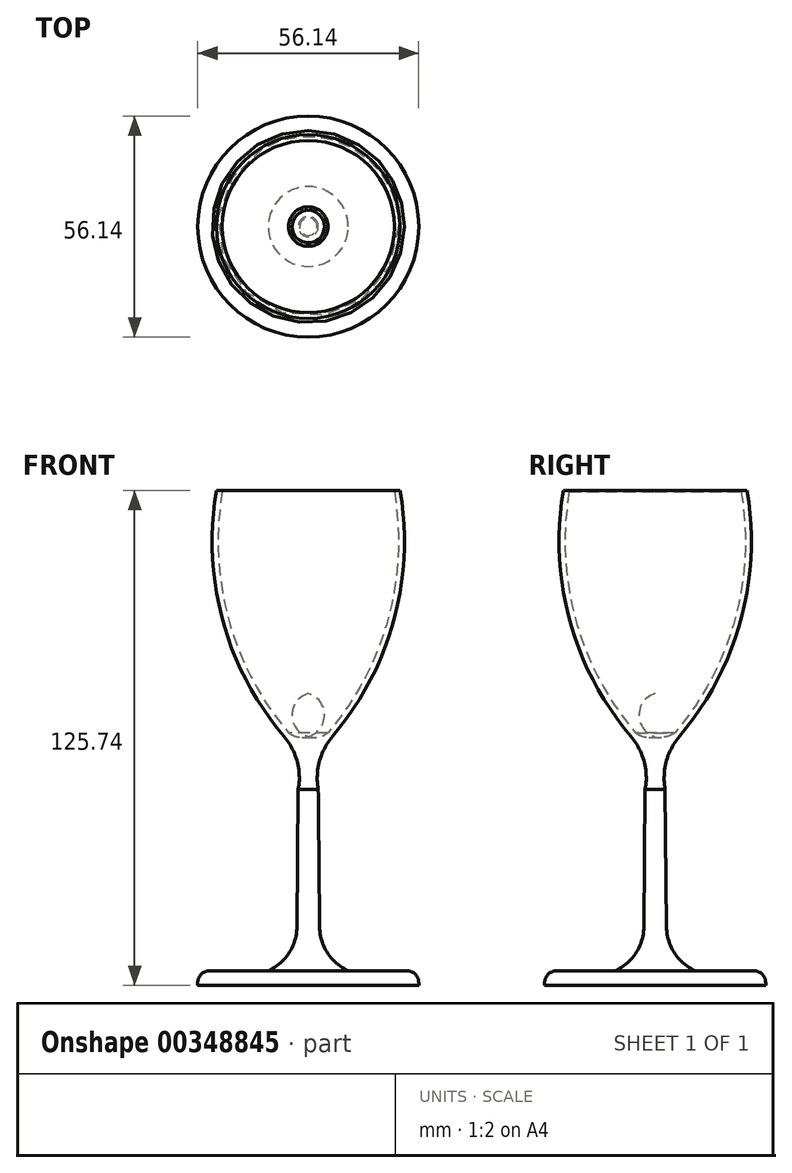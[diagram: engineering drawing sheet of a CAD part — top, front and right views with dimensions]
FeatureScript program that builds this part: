
annotation { "Feature Type Name" : "Feature", "Feature Type Description" : "" }
export const myFeature = defineFeature(function(context is Context, id is Id, definition is map)
    precondition{}
    {
        {
            var Q0;
            Q0=qCreatedBy(makeId("Front.planeOp"),FACE);
            var sketch = newSketch(context, id + "F0", { "sketchPlane" : qUnion([Q0])});
            skArc(sketch, "E0", {"start": v(6.16, -12.1) * mm, "mid": v(21.68, 17.25) * mm, "end": v(23.33, 50.4) * mm});
            skArc(sketch, "E1", {"start": v(6.16, -12.1) * mm, "mid": v(2.83, -18.42) * mm, "end": v(2.54, -25.57) * mm});
            skLineSegment(sketch, "E2", {"start": v(2.88, -60.4) * mm, "end": v(2.54, -25.57) * mm});
            skArc(sketch, "E3", {"start": v(2.88, -60.4) * mm, "mid": v(4.88, -67.06) * mm, "end": v(10.14, -71.62) * mm});
            skLineSegment(sketch, "E4", {"start": v(10.14, -71.62) * mm, "end": v(28.07, -71.62) * mm});
            skLineSegment(sketch, "E5", {"start": v(28.07, -71.62) * mm, "end": v(28.07, -75.33) * mm});
            skLineSegment(sketch, "E6", {"start": v(28.07, -75.33) * mm, "end": v(0, -75.33) * mm});
            skArc(sketch, "E7.0", {"start": v(5.01, -11.12) * mm, "mid": v(20.24, 17.65) * mm, "end": v(21.85, 50.16) * mm});
            skLineSegment(sketch, "E8", {"start": v(21.85, 50.16) * mm, "end": v(23.33, 50.4) * mm});
            skArc(sketch, "E9", {"start": v(0, -12.1) * mm, "mid": v(2.62, -12.2) * mm, "end": v(5.01, -11.12) * mm});
            skLineSegment(sketch, "E10", {"start": v(0, -12.1) * mm, "end": v(0, -75.33) * mm});
            skLineSegment(sketch, "E11", {"start": v(0, 71.66) * mm, "end": v(0, -120.18) * mm, "construction": true});
            skSolve(sketch);
        }
        {
            var Q0;
            Q0=qCreatedBy(makeId("Front.planeOp"),FACE);
            var sketch = newSketch(context, id + "F1", { "sketchPlane" : qUnion([Q0])});
            skLineSegment(sketch, "E12", {"start": v(0, 118.6) * mm, "end": v(0, -104.37) * mm, "construction": true});
            skSolve(sketch);
        }
        {
            var Q0;
            Q0=makeQuery(id+"F0.imprint","IMPRINT",FACE,{"disambiguationData":[TD([[makeQuery(id+"F0.imprint","IMPRINT",EDGE,{"derivedFrom":sQuery(id+"F0.wireOp",EDGE,"E0")}),1.0]])]});
            var Q1;
            Q1=sQuery(id+"F1.wireOp",EDGE,"E12");
            revolve(context, id + "F2", {"entities" : qUnion([Q0]), "axis" : qUnion([Q1]), "revolveType" : RevolveType.FULL});
        }
        {
            var Q0;
            Q0=makeQuery(id+"F2.opRevolve","SWEPT_EDGE",EDGE,{"disambiguationData":[OSD([sQuery(id+"F0.wireOp",EDGE,"E4"),sQuery(id+"F0.wireOp",EDGE,"E5")])]});
            fillet(context, id + "F3", {"entities" : qUnion([Q0]), "radius" : 3 * mm, "tangentPropagation" : true, "allowEdgeOverflow" : false});
        }
    });
